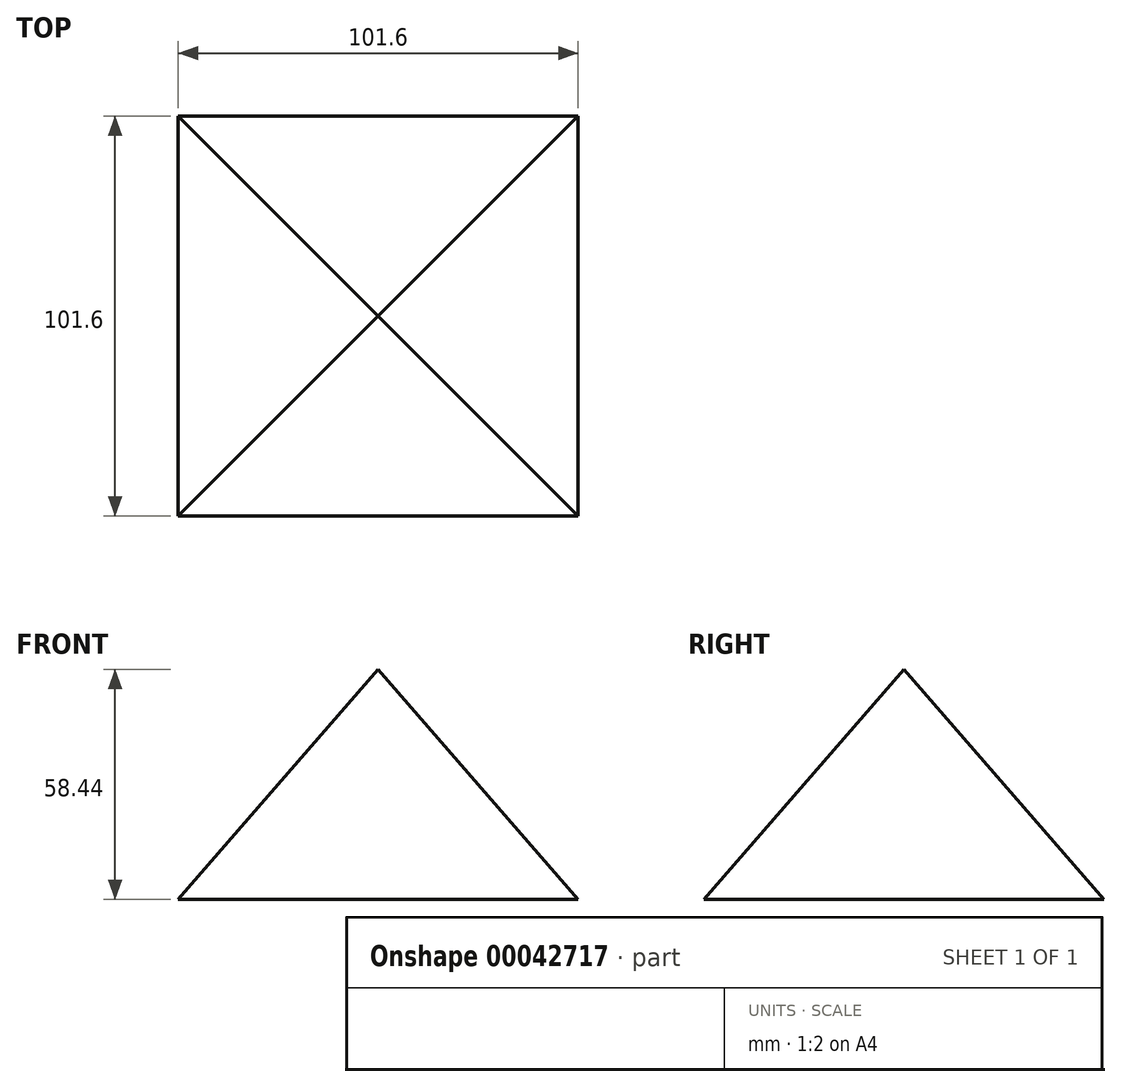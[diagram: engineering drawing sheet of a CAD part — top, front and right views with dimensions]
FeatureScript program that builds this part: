
annotation { "Feature Type Name" : "Feature", "Feature Type Description" : "" }
export const myFeature = defineFeature(function(context is Context, id is Id, definition is map)
    precondition{}
    {
        {
            var Q0;
            Q0=qCreatedBy(makeId("Top.planeOp"),FACE);
            var sketch = newSketch(context, id + "F0", { "sketchPlane" : qUnion([Q0])});
            skLineSegment(sketch, "E0.rect.bottom", {"start": v(50.8, 50.8) * mm, "end": v(-50.8, 50.8) * mm});
            skLineSegment(sketch, "E0.rect.top", {"start": v(50.8, -50.8) * mm, "end": v(-50.8, -50.8) * mm});
            skLineSegment(sketch, "E0.rect.left", {"start": v(50.8, 50.8) * mm, "end": v(50.8, -50.8) * mm});
            skLineSegment(sketch, "E0.rect.right", {"start": v(-50.8, 50.8) * mm, "end": v(-50.8, -50.8) * mm});
            skPoint(sketch, "E0.rect.middle", {"position": v(0, 0) * mm});
            skSolve(sketch);
        }
        {
            var Q0;
            Q0=makeQuery(id+"F0.imprint","IMPRINT",FACE,{"disambiguationData":[TD([[makeQuery(id+"F0.imprint","IMPRINT",EDGE,{"derivedFrom":sQuery(id+"F0.wireOp",EDGE,"E0.rect.bottom")}),1.0]])]});
            extrude(context, id + "F1", {"entities" : qUnion([Q0]), "depth" : 108.13 * mm, "hasDraft" : true, "draftAngle" : 41 * degree, "draftPullDirection" : true});
        }
    });
